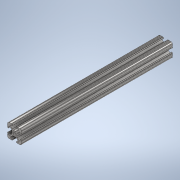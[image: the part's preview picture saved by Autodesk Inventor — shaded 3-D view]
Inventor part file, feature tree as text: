
AUTODESK INVENTOR PART (.ipt)
format: ipt  version: 2020 (Build 240168000, 168)  size: 239,104 bytes
history: native  units: in
note: dims shown in document units (in); Inventor stores cm internally (conversion verified against a paired STEP export)
features: extrude x1, sketch x1
ambient origin geometry x8: Origin, YZ Plane, XZ Plane, XY Plane, X Axis, Y Axis, Z Axis, Center Point
bodies: Solid1 (feature_tree)
feature tree (2):
  extrude  "Extrusion1"  [1 undecoded]
  sketch  "Sketch1"  dims[d0=11.0in d1=0.0in]
note: 1 required parameter value undecoded (feature->parameter linkage not recoverable at this tier; creation-order binding heuristic only, values carry confidence <= 0.55)
